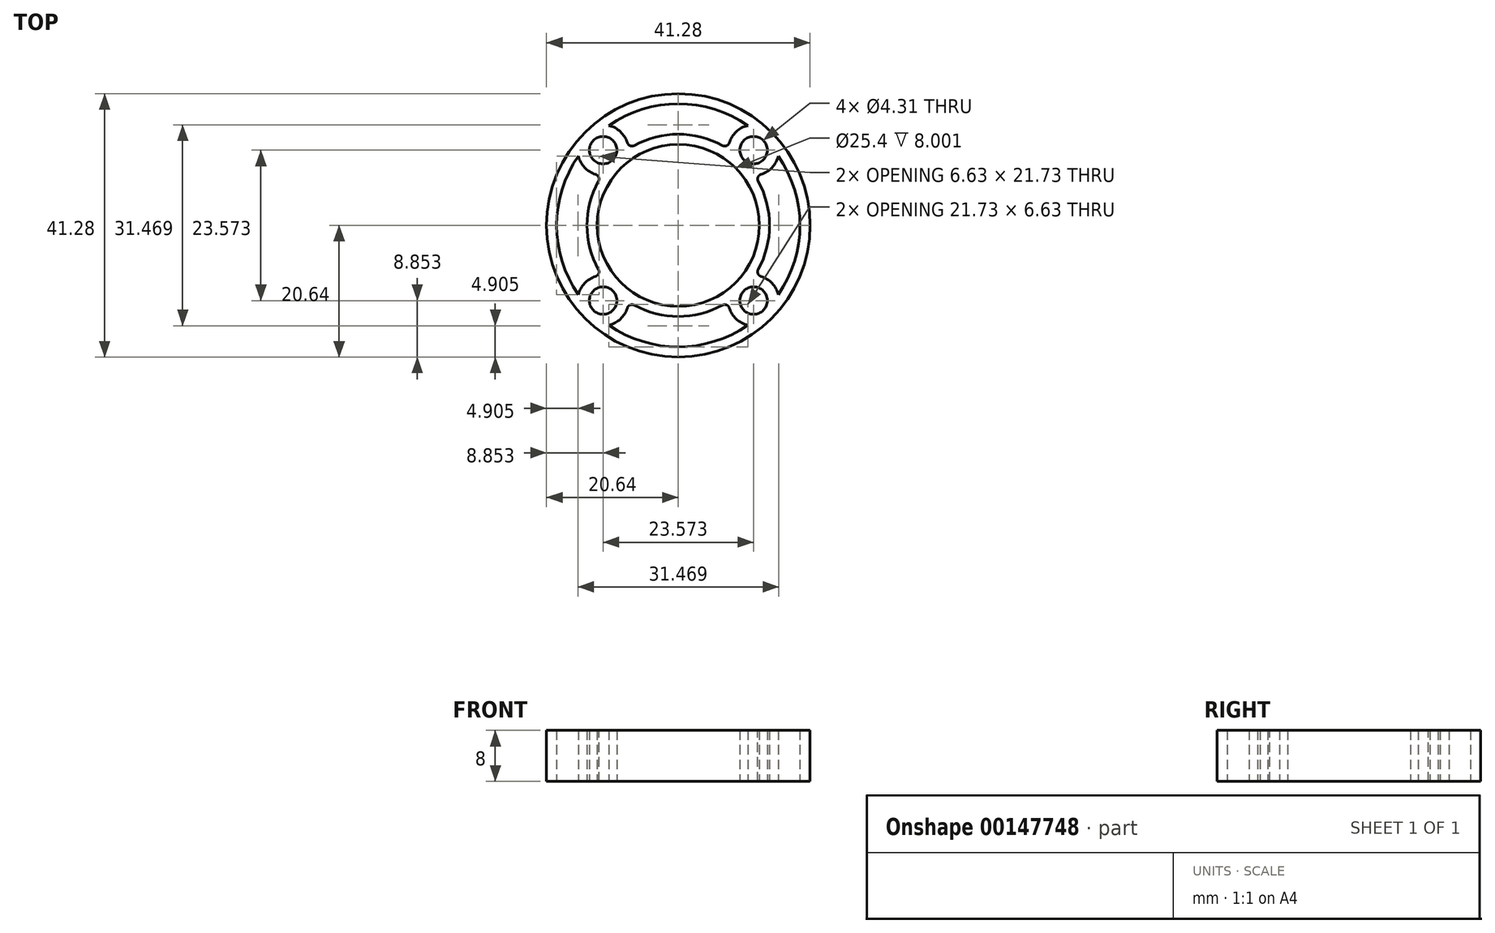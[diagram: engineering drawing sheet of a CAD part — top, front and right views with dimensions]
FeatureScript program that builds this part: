
annotation { "Feature Type Name" : "Feature", "Feature Type Description" : "" }
export const myFeature = defineFeature(function(context is Context, id is Id, definition is map)
    precondition{}
    {
        {
            var Q0;
            Q0=qCreatedBy(makeId("Top.planeOp"),FACE);
            var sketch = newSketch(context, id + "F0", { "sketchPlane" : qUnion([Q0])});
            skCircle(sketch, "E0", {"center": v(0, 0) * mm, "radius": 12.7 * mm});
            skLineSegment(sketch, "E1.bottom", {"start": v(11.79, 11.79) * mm, "end": v(-11.79, 11.79) * mm, "construction": true});
            skLineSegment(sketch, "E1.top", {"start": v(11.79, -11.79) * mm, "end": v(-11.79, -11.79) * mm, "construction": true});
            skLineSegment(sketch, "E1.left", {"start": v(11.79, 11.79) * mm, "end": v(11.79, -11.79) * mm, "construction": true});
            skLineSegment(sketch, "E1.right", {"start": v(-11.79, 11.79) * mm, "end": v(-11.79, -11.79) * mm, "construction": true});
            skCircle(sketch, "E2", {"center": v(-11.79, 11.79) * mm, "radius": 3.97 * mm, "construction": true});
            skCircle(sketch, "E3", {"center": v(-11.79, 11.79) * mm, "radius": 2.15 * mm});
            skCircle(sketch, "E4", {"center": v(-11.79, -11.79) * mm, "radius": 2.15 * mm});
            skCircle(sketch, "E5", {"center": v(11.79, -11.79) * mm, "radius": 2.15 * mm});
            skCircle(sketch, "E6", {"center": v(11.79, 11.79) * mm, "radius": 2.15 * mm});
            skCircle(sketch, "E7", {"center": v(0, 0) * mm, "radius": 20.64 * mm});
            skSolve(sketch);
        }
        {
            var Q0;
            Q0=qSketchRegion(id+"F0",true);
            extrude(context, id + "F1", {"entities" : qUnion([Q0]), "depth" : 8 * mm});
        }
        {
            var Q0;
            Q0=makeQuery(id+"F1.opExtrude","CAP_FACE",FACE,{"disambiguationData":[OSD([sQuery(id+"F0.wireOp",EDGE,"E0"),sQuery(id+"F0.wireOp",EDGE,"E3"),sQuery(id+"F0.wireOp",EDGE,"E4"),sQuery(id+"F0.wireOp",EDGE,"E5"),sQuery(id+"F0.wireOp",EDGE,"E6"),sQuery(id+"F0.wireOp",EDGE,"E7")])],"isStart":true});
            var sketch = newSketch(context, id + "F2", { "sketchPlane" : qUnion([Q0])});
            skArc(sketch, "E8", {"start": v(7.82, -11.96) * mm, "mid": v(8.73, -14.31) * mm, "end": v(10.87, -15.65) * mm});
            skArc(sketch, "E9", {"start": v(-10.87, -15.65) * mm, "mid": v(0, -19.05) * mm, "end": v(10.87, -15.65) * mm});
            skArc(sketch, "E10", {"start": v(-7.82, -11.96) * mm, "mid": v(0, -14.29) * mm, "end": v(7.82, -11.96) * mm});
            skArc(sketch, "E11", {"start": v(-10.87, -15.65) * mm, "mid": v(-8.73, -14.31) * mm, "end": v(-7.82, -11.96) * mm});
            skSolve(sketch);
        }
        {
            var Q0;
            Q0=qSketchRegion(id+"F2",true);
            var Q1;
            Q1=makeQuery(id+"F1.opExtrude","CAP_FACE",FACE,{"disambiguationData":[OSD([sQuery(id+"F0.wireOp",EDGE,"E0"),sQuery(id+"F0.wireOp",EDGE,"E3"),sQuery(id+"F0.wireOp",EDGE,"E4"),sQuery(id+"F0.wireOp",EDGE,"E5"),sQuery(id+"F0.wireOp",EDGE,"E6"),sQuery(id+"F0.wireOp",EDGE,"E7")])],"isStart":false});
            extrude(context, id + "F3", {"entities" : qUnion([Q0]), "operationType" : NewBodyOperationType.REMOVE, "endBound" : BoundingType.UP_TO_SURFACE, "oppositeDirection" : true, "endBoundEntityFace" : qUnion([Q1]), "depth" : 25.4 * mm});
        }
        {
            var Q0;
            Q0=makeQuery(id+"F3.boolean.opBoolean","COPY",FACE,{"derivedFrom":makeQuery(id+"F3.opExtrude","SWEPT_FACE",FACE,{"disambiguationData":[OSD([sQuery(id+"F2.wireOp",EDGE,"E9")])]})});
            var Q1;
            Q1=makeQuery(id+"F3.boolean.opBoolean","COPY",FACE,{"derivedFrom":makeQuery(id+"F3.opExtrude","SWEPT_FACE",FACE,{"disambiguationData":[OSD([sQuery(id+"F2.wireOp",EDGE,"E11")])]})});
            var Q2;
            Q2=makeQuery(id+"F3.boolean.opBoolean","COPY",FACE,{"derivedFrom":makeQuery(id+"F3.opExtrude","SWEPT_FACE",FACE,{"disambiguationData":[OSD([sQuery(id+"F2.wireOp",EDGE,"E10")])]})});
            var Q3;
            Q3=makeQuery(id+"F3.boolean.opBoolean","COPY",FACE,{"derivedFrom":makeQuery(id+"F3.opExtrude","SWEPT_FACE",FACE,{"disambiguationData":[OSD([sQuery(id+"F2.wireOp",EDGE,"E8")])]})});
            var Q4;
            Q4=makeQuery(id+"F1.opExtrude","SWEPT_FACE",FACE,{"disambiguationData":[OSD([sQuery(id+"F0.wireOp",EDGE,"E7")])]});
            circularPattern(context, id + "F4", {"patternType" : PatternType.FACE, "faces" : qUnion([Q0, Q1, Q2, Q3]), "axis" : qUnion([Q4]), "angle" : 90 * degree, "instanceCount" : 4});
        }
        {
            var Q0;
            Q0=makeQuery(id+"F3.boolean.opBoolean","COPY",EDGE,{"derivedFrom":makeQuery(id+"F3.opExtrude","SWEPT_EDGE",EDGE,{"disambiguationData":[OSD([sQuery(id+"F2.wireOp",EDGE,"E10"),sQuery(id+"F2.wireOp",EDGE,"E11")])]})});
            var Q1;
            Q1=makeQuery(id+"F3.boolean.opBoolean","COPY",EDGE,{"derivedFrom":makeQuery(id+"F3.opExtrude","SWEPT_EDGE",EDGE,{"disambiguationData":[OSD([sQuery(id+"F2.wireOp",EDGE,"E8"),sQuery(id+"F2.wireOp",EDGE,"E10")])]})});
            var Q2;
            Q2=makeQuery(id+"F4.opPattern","COPY",EDGE,{"derivedFrom":makeQuery(id+"F3.boolean.opBoolean","COPY",EDGE,{"derivedFrom":makeQuery(id+"F3.opExtrude","SWEPT_EDGE",EDGE,{"disambiguationData":[OSD([sQuery(id+"F2.wireOp",EDGE,"E10"),sQuery(id+"F2.wireOp",EDGE,"E11")])]})}),"instanceName":"3"});
            var Q3;
            Q3=makeQuery(id+"F4.opPattern","COPY",EDGE,{"derivedFrom":makeQuery(id+"F3.boolean.opBoolean","COPY",EDGE,{"derivedFrom":makeQuery(id+"F3.opExtrude","SWEPT_EDGE",EDGE,{"disambiguationData":[OSD([sQuery(id+"F2.wireOp",EDGE,"E8"),sQuery(id+"F2.wireOp",EDGE,"E10")])]})}),"instanceName":"3"});
            var Q4;
            Q4=makeQuery(id+"F4.opPattern","COPY",EDGE,{"derivedFrom":makeQuery(id+"F3.boolean.opBoolean","COPY",EDGE,{"derivedFrom":makeQuery(id+"F3.opExtrude","SWEPT_EDGE",EDGE,{"disambiguationData":[OSD([sQuery(id+"F2.wireOp",EDGE,"E8"),sQuery(id+"F2.wireOp",EDGE,"E10")])]})}),"instanceName":"2"});
            var Q5;
            Q5=makeQuery(id+"F4.opPattern","COPY",EDGE,{"derivedFrom":makeQuery(id+"F3.boolean.opBoolean","COPY",EDGE,{"derivedFrom":makeQuery(id+"F3.opExtrude","SWEPT_EDGE",EDGE,{"disambiguationData":[OSD([sQuery(id+"F2.wireOp",EDGE,"E10"),sQuery(id+"F2.wireOp",EDGE,"E11")])]})}),"instanceName":"2"});
            var Q6;
            Q6=makeQuery(id+"F4.opPattern","COPY",EDGE,{"derivedFrom":makeQuery(id+"F3.boolean.opBoolean","COPY",EDGE,{"derivedFrom":makeQuery(id+"F3.opExtrude","SWEPT_EDGE",EDGE,{"disambiguationData":[OSD([sQuery(id+"F2.wireOp",EDGE,"E10"),sQuery(id+"F2.wireOp",EDGE,"E11")])]})}),"instanceName":"1"});
            var Q7;
            Q7=makeQuery(id+"F4.opPattern","COPY",EDGE,{"derivedFrom":makeQuery(id+"F3.boolean.opBoolean","COPY",EDGE,{"derivedFrom":makeQuery(id+"F3.opExtrude","SWEPT_EDGE",EDGE,{"disambiguationData":[OSD([sQuery(id+"F2.wireOp",EDGE,"E8"),sQuery(id+"F2.wireOp",EDGE,"E10")])]})}),"instanceName":"1"});
            fillet(context, id + "F5", {"entities" : qUnion([Q0, Q1, Q2, Q3, Q4, Q5, Q6, Q7]), "radius" : 0.76 * mm, "tangentPropagation" : true, "allowEdgeOverflow" : false});
        }
    });
